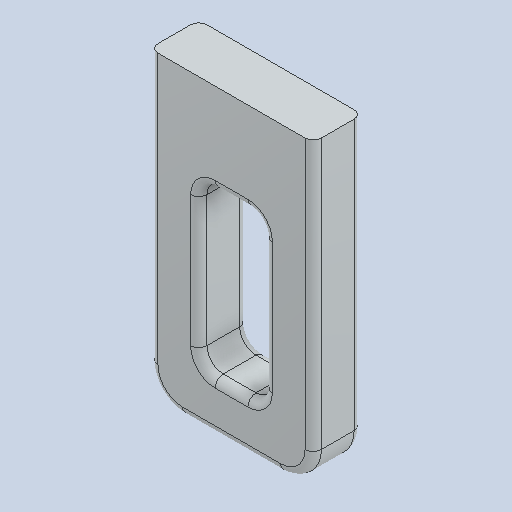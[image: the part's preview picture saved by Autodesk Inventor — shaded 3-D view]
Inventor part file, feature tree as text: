
AUTODESK INVENTOR PART (.ipt)
format: ipt  version: 2025.1 (Build 291241020, 241B)  size: 140,800 bytes
history: native  units: in
note: dims shown in document units (in); Inventor stores cm internally (conversion verified against a paired STEP export)
features: fillet x1
ambient origin geometry x8: Origin, YZ Plane, XZ Plane, XY Plane, X Axis, Y Axis, Z Axis, Center Point
bodies: Solid1 (feature_tree)
feature tree (1):
  fillet  "Fillet3"  [1 undecoded]
note: 1 required parameter value undecoded (feature->parameter linkage not recoverable at this tier; creation-order binding heuristic only, values carry confidence <= 0.55)
